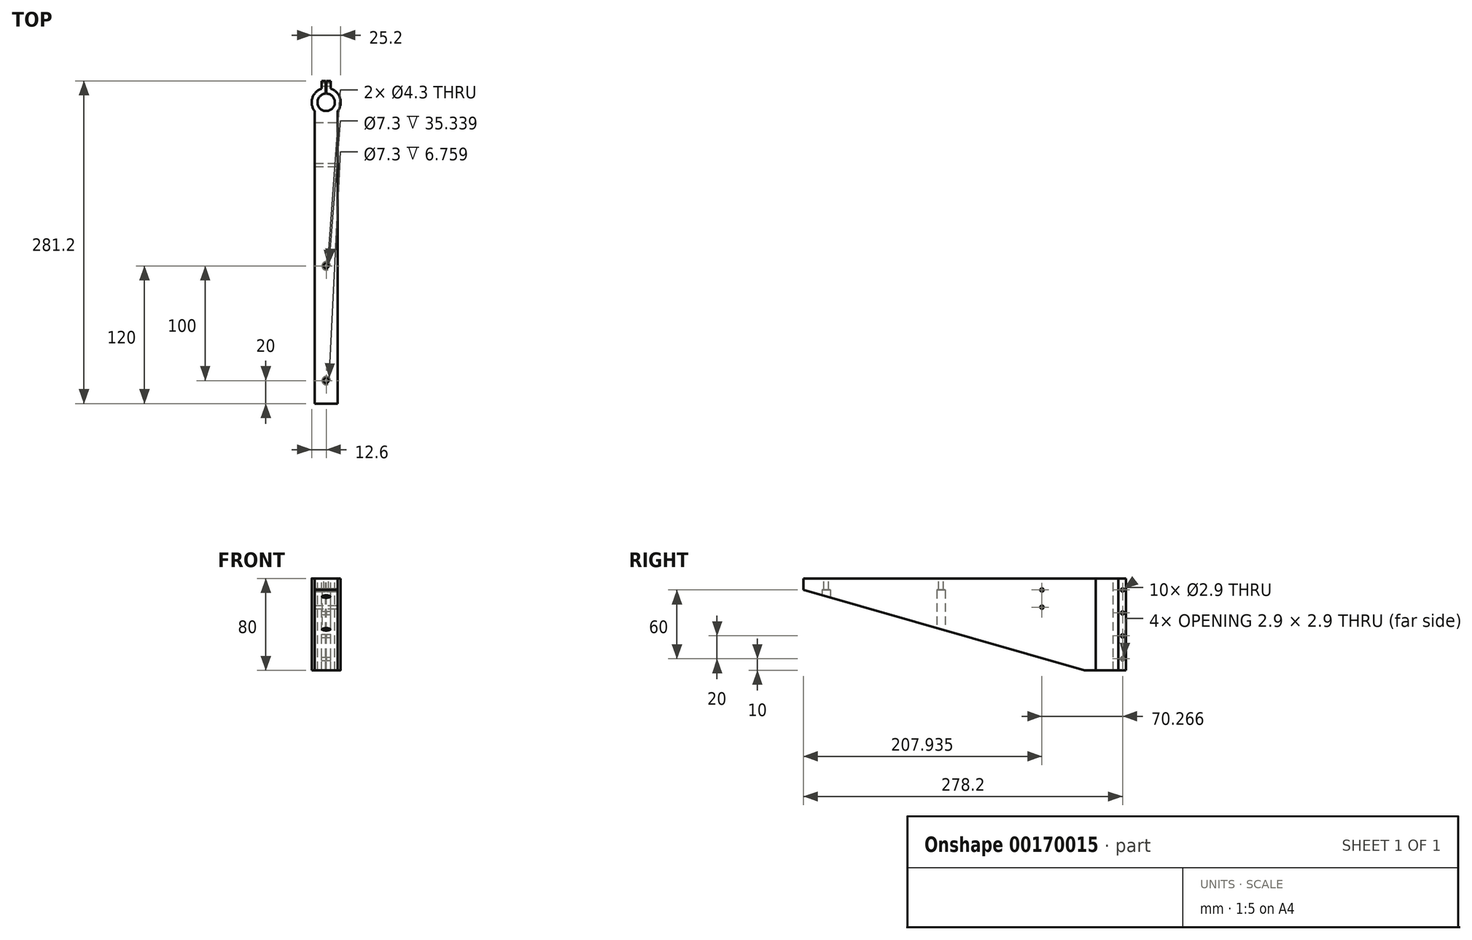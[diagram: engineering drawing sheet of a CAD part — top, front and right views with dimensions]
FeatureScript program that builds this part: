
annotation { "Feature Type Name" : "Feature", "Feature Type Description" : "" }
export const myFeature = defineFeature(function(context is Context, id is Id, definition is map)
    precondition{}
    {
        {
            var Q0;
            Q0=qCreatedBy(makeId("Top.planeOp"),FACE);
            var sketch = newSketch(context, id + "F0", { "sketchPlane" : qUnion([Q0])});
            skCircle(sketch, "E0", {"center": v(0, 0) * mm, "radius": 7.6 * mm});
            skArc(sketch, "E1.0", {"start": v(-4, 11.95) * mm, "mid": v(0, -12.6) * mm, "end": v(4, 11.95) * mm});
            skLineSegment(sketch, "E2.top", {"start": v(4, 18.6) * mm, "end": v(-4, 18.6) * mm});
            skLineSegment(sketch, "E2.left", {"start": v(4, 11.95) * mm, "end": v(4, 18.6) * mm});
            skLineSegment(sketch, "E2.right", {"start": v(-4, 11.95) * mm, "end": v(-4, 18.6) * mm});
            skPoint(sketch, "E2.middle", {"position": v(0, 12.6) * mm});
            skLineSegment(sketch, "E3.top", {"start": v(-10, -262.6) * mm, "end": v(10, -262.6) * mm});
            skLineSegment(sketch, "E3.left", {"start": v(-10, -7.67) * mm, "end": v(-10, -262.6) * mm});
            skLineSegment(sketch, "E3.right", {"start": v(10, -7.67) * mm, "end": v(10, -262.6) * mm});
            skSolve(sketch);
        }
        {
            var Q0;
            Q0=makeQuery(id+"F0.imprint","IMPRINT",FACE,{"disambiguationData":[TD([[makeQuery(id+"F0.imprint","IMPRINT",EDGE,{"derivedFrom":sQuery(id+"F0.wireOp",EDGE,"E3.top")}),1.0]])]});
            extrude(context, id + "F1", {"entities" : qUnion([Q0]), "oppositeDirection" : true, "depth" : 80 * mm});
        }
        {
            var Q0;
            Q0=makeQuery(id+"F0.imprint","IMPRINT",FACE,{"disambiguationData":[TD([[makeQuery(id+"F0.imprint","IMPRINT",EDGE,{"derivedFrom":sQuery(id+"F0.wireOp",EDGE,"E0")}),-1.0]])]});
            extrude(context, id + "F2", {"entities" : qUnion([Q0]), "operationType" : NewBodyOperationType.ADD, "oppositeDirection" : true, "depth" : 80 * mm});
        }
        {
            var Q0;
            {var subQ0=sQuery(id+"F0.wireOp",EDGE,"E1.0");Q0=makeQuery(id+"F2.boolean.opBoolean","MERGE",FACE,{"derivedFrom":[makeQuery(id+"F1.opExtrude","CAP_FACE",FACE,{"disambiguationData":[OSD([subQ0,sQuery(id+"F0.wireOp",EDGE,"E3.top"),sQuery(id+"F0.wireOp",EDGE,"E3.left"),sQuery(id+"F0.wireOp",EDGE,"E3.right")])],"isStart":true}),makeQuery(id+"F2.opExtrude","CAP_FACE",FACE,{"disambiguationData":[OSD([sQuery(id+"F0.wireOp",EDGE,"E0"),subQ0,sQuery(id+"F0.wireOp",EDGE,"E2.top"),sQuery(id+"F0.wireOp",EDGE,"E2.left"),sQuery(id+"F0.wireOp",EDGE,"E2.right")])],"isStart":true})]});}
            var sketch = newSketch(context, id + "F3", { "sketchPlane" : qUnion([Q0])});
            skCircle(sketch, "E4", {"center": v(0, -142.6) * mm, "radius": 2.15 * mm});
            skCircle(sketch, "E5", {"center": v(0, -242.6) * mm, "radius": 2.15 * mm});
            skSolve(sketch);
        }
        {
            var Q0;
            Q0=qSketchRegion(id+"F3",true);
            extrude(context, id + "F4", {"entities" : qUnion([Q0]), "operationType" : NewBodyOperationType.REMOVE, "endBound" : BoundingType.THROUGH_ALL, "oppositeDirection" : true, "depth" : 25 * mm});
        }
        {
            var Q0;
            Q0=makeQuery(id+"F1.opExtrude","CAP_FACE",FACE,{"disambiguationData":[OSD([sQuery(id+"F0.wireOp",EDGE,"E0"),sQuery(id+"F0.wireOp",EDGE,"E1.0"),sQuery(id+"F0.wireOp",EDGE,"E2.top"),sQuery(id+"F0.wireOp",EDGE,"E2.left"),sQuery(id+"F0.wireOp",EDGE,"E2.right"),sQuery(id+"F0.wireOp",EDGE,"E3.top"),sQuery(id+"F0.wireOp",EDGE,"E3.left"),sQuery(id+"F0.wireOp",EDGE,"E3.right")])],"isStart":false});
            var sketch = newSketch(context, id + "F5", { "sketchPlane" : qUnion([Q0])});
            skCircle(sketch, "E6", {"center": v(0, 242.6) * mm, "radius": 3.65 * mm});
            skCircle(sketch, "E7", {"center": v(0, 142.6) * mm, "radius": 3.65 * mm});
            skSolve(sketch);
        }
        {
            var Q0;
            Q0=makeQuery(id+"F5.imprint","IMPRINT",FACE,{"disambiguationData":[TD([[makeQuery(id+"F5.imprint","IMPRINT",EDGE,{"derivedFrom":sQuery(id+"F5.wireOp",EDGE,"E6")}),1.0]])]});
            var Q1;
            Q1=makeQuery(id+"F5.imprint","IMPRINT",FACE,{"disambiguationData":[TD([[makeQuery(id+"F5.imprint","IMPRINT",EDGE,{"derivedFrom":sQuery(id+"F5.wireOp",EDGE,"E7")}),1.0]])]});
            extrude(context, id + "F6", {"entities" : qUnion([Q0, Q1]), "operationType" : NewBodyOperationType.REMOVE, "oppositeDirection" : true, "depth" : (80 - 10) * mm});
        }
        {
            var Q0;
            Q0=makeQuery(id+"F1.opExtrude","SWEPT_FACE",FACE,{"disambiguationData":[OSD([sQuery(id+"F0.wireOp",EDGE,"E3.right")])]});
            var sketch = newSketch(context, id + "F7", { "sketchPlane" : qUnion([Q0])});
            skLineSegment(sketch, "E8", {"start": v(-7.67, -80) * mm, "end": v(-17.67, -80) * mm});
            skLineSegment(sketch, "E9", {"start": v(-262.6, 0) * mm, "end": v(-262.6, -10) * mm});
            skEllipse(sketch, "E10", {"center": v(-262.6, -80) * mm, "majorRadius": 247.08 * mm, "minorRadius": 90 * mm, "majorAxis": v(1, 0), "construction": true});
            skLineSegment(sketch, "E11", {"start": v(-17.67, -80) * mm, "end": v(-262.6, -10) * mm});
            skSolve(sketch);
        }
        {
            var Q0;
            {var subQ1=sQuery(id+"F0.wireOp",EDGE,"E3.right");var subQ2=makeQuery(id+"F1.opExtrude","SWEPT_EDGE",EDGE,{"disambiguationData":[OSD([sQuery(id+"F0.wireOp",EDGE,"E3.top"),subQ1])]});var subQ4=makeQuery(id+"F1.opExtrude","CAP_EDGE",EDGE,{"disambiguationData":[OSD([subQ1])],"isStart":false});var subQ6=makeQuery(id+"F7.imprint","INTERSECT",VERTEX,{"derivedFrom":[subQ2,subQ4]});Q0=makeQuery(id+"F7.imprint","IMPRINT",FACE,{"disambiguationData":[TD([[makeQuery(id+"F7.imprint","IMPRINT",EDGE,{"disambiguationData":[TD([[subQ6,1.0]])],"derivedFrom":subQ4}),-1.0]])]});}
            extrude(context, id + "F8", {"entities" : qUnion([Q0]), "operationType" : NewBodyOperationType.REMOVE, "endBound" : BoundingType.THROUGH_ALL, "oppositeDirection" : true, "depth" : 25 * mm});
        }
        {
            var Q0;
            Q0=makeQuery(id+"F1.opExtrude","CAP_FACE",FACE,{"disambiguationData":[OSD([sQuery(id+"F0.wireOp",EDGE,"E0"),sQuery(id+"F0.wireOp",EDGE,"E1.0"),sQuery(id+"F0.wireOp",EDGE,"E2.top"),sQuery(id+"F0.wireOp",EDGE,"E2.left"),sQuery(id+"F0.wireOp",EDGE,"E2.right"),sQuery(id+"F0.wireOp",EDGE,"E3.top"),sQuery(id+"F0.wireOp",EDGE,"E3.left"),sQuery(id+"F0.wireOp",EDGE,"E3.right")])],"isStart":true});
            var sketch = newSketch(context, id + "F9", { "sketchPlane" : qUnion([Q0])});
            skLineSegment(sketch, "E12.bottom", {"start": v(0, 18.6) * mm, "end": v(-0.5, 18.6) * mm});
            skLineSegment(sketch, "E12.top", {"start": v(0, 0) * mm, "end": v(-0.5, 0) * mm});
            skLineSegment(sketch, "E12.left", {"start": v(0, 18.6) * mm, "end": v(0, 0) * mm});
            skLineSegment(sketch, "E12.right", {"start": v(-0.5, 18.6) * mm, "end": v(-0.5, 0) * mm});
            skLineSegment(sketch, "E13.MirrorCS", {"start": v(0.5, 18.6) * mm, "end": v(0.5, 0) * mm});
            skLineSegment(sketch, "E14.MirrorCS", {"start": v(0, 0) * mm, "end": v(0.5, 0) * mm});
            skLineSegment(sketch, "E15.MirrorCS", {"start": v(0, 18.6) * mm, "end": v(0.5, 18.6) * mm});
            skSolve(sketch);
        }
        {
            var Q0;
            {var subQ0=sQuery(id+"F9.wireOp",EDGE,"E12.left");var subQ1=makeQuery(id+"F2.opExtrude","CAP_EDGE",EDGE,{"disambiguationData":[OSD([sQuery(id+"F0.wireOp",EDGE,"E2.top")])],"isStart":true});var subQ2=makeQuery(id+"F9.imprint","INTERSECT",VERTEX,{"derivedFrom":[subQ1,subQ0]});Q0=makeQuery(id+"F9.imprint","IMPRINT",FACE,{"disambiguationData":[TD([[makeQuery(id+"F9.imprint","IMPRINT",EDGE,{"disambiguationData":[TD([[subQ2,-1.0]])],"derivedFrom":subQ0}),1.0]])]});}
            var Q1;
            {var subQ0=sQuery(id+"F9.wireOp",EDGE,"E12.top");Q1=makeQuery(id+"F9.imprint","IMPRINT",FACE,{"disambiguationData":[TD([[makeQuery(id+"F9.imprint","IMPRINT",EDGE,{"derivedFrom":subQ0}),-1.0]])]});}
            var Q2;
            {var subQ0=sQuery(id+"F9.wireOp",EDGE,"E12.bottom");Q2=makeQuery(id+"F9.imprint","IMPRINT",FACE,{"disambiguationData":[TD([[makeQuery(id+"F9.imprint","IMPRINT",EDGE,{"derivedFrom":subQ0}),1.0]])]});}
            var Q3;
            {var subQ0=sQuery(id+"F9.wireOp",EDGE,"E15.MirrorCS");Q3=makeQuery(id+"F9.imprint","IMPRINT",FACE,{"disambiguationData":[TD([[makeQuery(id+"F9.imprint","IMPRINT",EDGE,{"derivedFrom":subQ0}),-1.0]])]});}
            var Q4;
            {var subQ0=sQuery(id+"F9.wireOp",EDGE,"E14.MirrorCS");Q4=makeQuery(id+"F9.imprint","IMPRINT",FACE,{"disambiguationData":[TD([[makeQuery(id+"F9.imprint","IMPRINT",EDGE,{"derivedFrom":subQ0}),1.0]])]});}
            var Q5;
            {var subQ0=sQuery(id+"F9.wireOp",EDGE,"E12.left");var subQ1=makeQuery(id+"F2.opExtrude","CAP_EDGE",EDGE,{"disambiguationData":[OSD([sQuery(id+"F0.wireOp",EDGE,"E2.top")])],"isStart":true});var subQ2=makeQuery(id+"F9.imprint","INTERSECT",VERTEX,{"derivedFrom":[subQ1,subQ0]});Q5=makeQuery(id+"F9.imprint","IMPRINT",FACE,{"disambiguationData":[TD([[makeQuery(id+"F9.imprint","IMPRINT",EDGE,{"disambiguationData":[TD([[subQ2,-1.0]])],"derivedFrom":subQ0}),-1.0]])]});}
            extrude(context, id + "F10", {"entities" : qUnion([Q0, Q1, Q2, Q3, Q4, Q5]), "operationType" : NewBodyOperationType.REMOVE, "endBound" : BoundingType.THROUGH_ALL, "oppositeDirection" : true, "depth" : 25 * mm});
        }
        {
            var Q0;
            Q0=makeQuery(id+"F2.opExtrude","SWEPT_FACE",FACE,{"disambiguationData":[OSD([sQuery(id+"F0.wireOp",EDGE,"E2.left")])]});
            var sketch = newSketch(context, id + "F11", { "sketchPlane" : qUnion([Q0])});
            skCircle(sketch, "E16", {"center": v(15.6, -30) * mm, "radius": 1.45 * mm});
            skCircle(sketch, "E17", {"center": v(15.6, -70) * mm, "radius": 1.45 * mm});
            skCircle(sketch, "E18.0", {"center": v(15.6, -30) * mm, "radius": 2.45 * mm});
            skCircle(sketch, "E19.0", {"center": v(15.6, -70) * mm, "radius": 2.45 * mm});
            skLineSegment(sketch, "E20", {"start": v(18.6, -40) * mm, "end": v(26.32, -40) * mm});
            skLineSegment(sketch, "E21", {"start": v(26.84, -40) * mm, "end": v(18.6, -40) * mm});
            skCircle(sketch, "E22", {"center": v(15.6, -10) * mm, "radius": 1.45 * mm});
            skCircle(sketch, "E23", {"center": v(15.6, -10) * mm, "radius": 2.45 * mm});
            skCircle(sketch, "E24", {"center": v(15.6, -50) * mm, "radius": 1.45 * mm});
            skCircle(sketch, "E25", {"center": v(15.6, -50) * mm, "radius": 2.45 * mm});
            skSolve(sketch);
        }
        {
            var Q0;
            Q0=makeQuery(id+"F11.imprint","IMPRINT",FACE,{"disambiguationData":[TD([[makeQuery(id+"F11.imprint","IMPRINT",EDGE,{"derivedFrom":sQuery(id+"F11.wireOp",EDGE,"E16")}),1.0]])]});
            var Q1;
            Q1=makeQuery(id+"F11.imprint","IMPRINT",FACE,{"disambiguationData":[TD([[makeQuery(id+"F11.imprint","IMPRINT",EDGE,{"derivedFrom":sQuery(id+"F11.wireOp",EDGE,"E17")}),1.0]])]});
            var Q2;
            Q2=makeQuery(id+"F11.imprint","IMPRINT",FACE,{"disambiguationData":[TD([[makeQuery(id+"F11.imprint","IMPRINT",EDGE,{"derivedFrom":sQuery(id+"F11.wireOp",EDGE,"E24")}),1.0]])]});
            var Q3;
            Q3=makeQuery(id+"F11.imprint","IMPRINT",FACE,{"disambiguationData":[TD([[makeQuery(id+"F11.imprint","IMPRINT",EDGE,{"derivedFrom":sQuery(id+"F11.wireOp",EDGE,"E22")}),1.0]])]});
            extrude(context, id + "F12", {"entities" : qUnion([Q0, Q1, Q2, Q3]), "operationType" : NewBodyOperationType.REMOVE, "endBound" : BoundingType.THROUGH_ALL, "oppositeDirection" : true, "depth" : 25 * mm});
        }
        {
            var Q0;
            Q0=makeQuery(id+"F1.opExtrude","SWEPT_FACE",FACE,{"disambiguationData":[OSD([sQuery(id+"F0.wireOp",EDGE,"E3.right")])]});
            var sketch = newSketch(context, id + "F13", { "sketchPlane" : qUnion([Q0])});
            skCircle(sketch, "E26", {"center": v(-54.67, -10) * mm, "radius": 1.45 * mm});
            skCircle(sketch, "E27", {"center": v(-54.67, -25) * mm, "radius": 1.45 * mm});
            skSolve(sketch);
        }
        {
            var Q0;
            Q0=makeQuery(id+"F13.imprint","IMPRINT",FACE,{"disambiguationData":[TD([[makeQuery(id+"F13.imprint","IMPRINT",EDGE,{"derivedFrom":sQuery(id+"F13.wireOp",EDGE,"E26")}),1.0]])]});
            var Q1;
            Q1=makeQuery(id+"F13.imprint","IMPRINT",FACE,{"disambiguationData":[TD([[makeQuery(id+"F13.imprint","IMPRINT",EDGE,{"derivedFrom":sQuery(id+"F13.wireOp",EDGE,"E27")}),1.0]])]});
            extrude(context, id + "F14", {"entities" : qUnion([Q0, Q1]), "operationType" : NewBodyOperationType.REMOVE, "endBound" : BoundingType.THROUGH_ALL, "oppositeDirection" : true, "depth" : 25 * mm});
        }
    });
